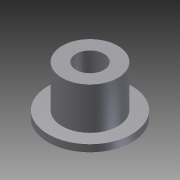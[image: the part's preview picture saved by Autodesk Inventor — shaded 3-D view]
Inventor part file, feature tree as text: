
AUTODESK INVENTOR PART (.ipt)
format: ipt  version: 2011 (Build 150239000, 239)  size: 86,528 bytes
history: native  units: mm
features: extrude x2, sketch x2, hole x1
ambient origin geometry x8: Origin, YZ Plane, XZ Plane, XY Plane, X Axis, Y Axis, Z Axis, Center Point
bodies: Solid1 (feature_tree)
feature tree (5):
  extrude  "Extrusion1"  Depth=0.5mm TaperAngle=0.0deg
  extrude  "Extrusion2"  Depth=3.0mm TaperAngle=0.0deg
  hole  "Hole1"  [1 undecoded]
  sketch  "Sketch1"  dims[d0=6.0mm d1=0.5mm d2=0.0mm]
  sketch  "Sketch2"  dims[d3=4.0mm d4=3.0mm d5=0.0mm d6=10.0mm d7=10.0mm d8=2.0mm d9=6.0mm d10=4.0mm d11=2.0mm d12=90.0deg d13=3.5mm d14=0.0mm]
note: 1 required parameter value undecoded (feature->parameter linkage not recoverable at this tier; creation-order binding heuristic only, values carry confidence <= 0.55)
